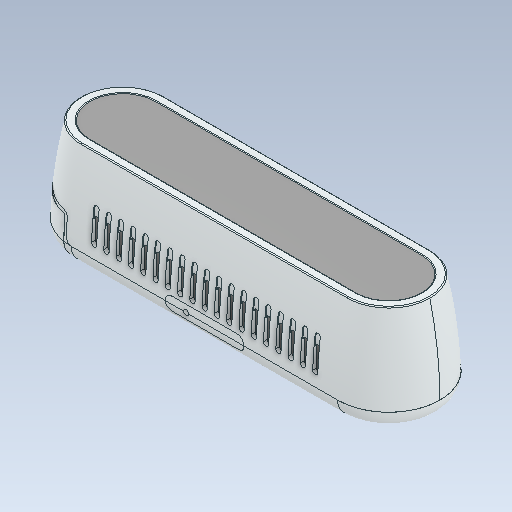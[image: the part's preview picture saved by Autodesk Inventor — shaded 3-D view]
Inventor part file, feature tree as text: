
AUTODESK INVENTOR PART (.ipt)
format: ipt  version: 2021 (Build 250183000, 183)  size: 1,199,616 bytes
history: mixed  units: mm
features: other x4, thread x1, imported_body x1
ambient origin geometry x8: Origin, YZ Plane, XZ Plane, XY Plane, X Axis, Y Axis, Z Axis, Center Point
bodies: Solid1 (imported_parasolid), Solid2 (imported_parasolid), Solid3 (imported_parasolid), Solid4 (imported_parasolid), Solid5 (imported_parasolid)
feature tree (6):
  other  "Split2[2]"
  thread  "Thread1"  [1 undecoded]
  other  "Cut-Extrude10[1]"
  other  "Cut-Extrude10[2]"
  other  "Cut-Extrude12"
  imported_body  NMx_Import_Brep_tag  [imported B-rep: ~21 faces, bbox_mm=None]
note: 1 required parameter value undecoded (feature->parameter linkage not recoverable at this tier; creation-order binding heuristic only, values carry confidence <= 0.55)
